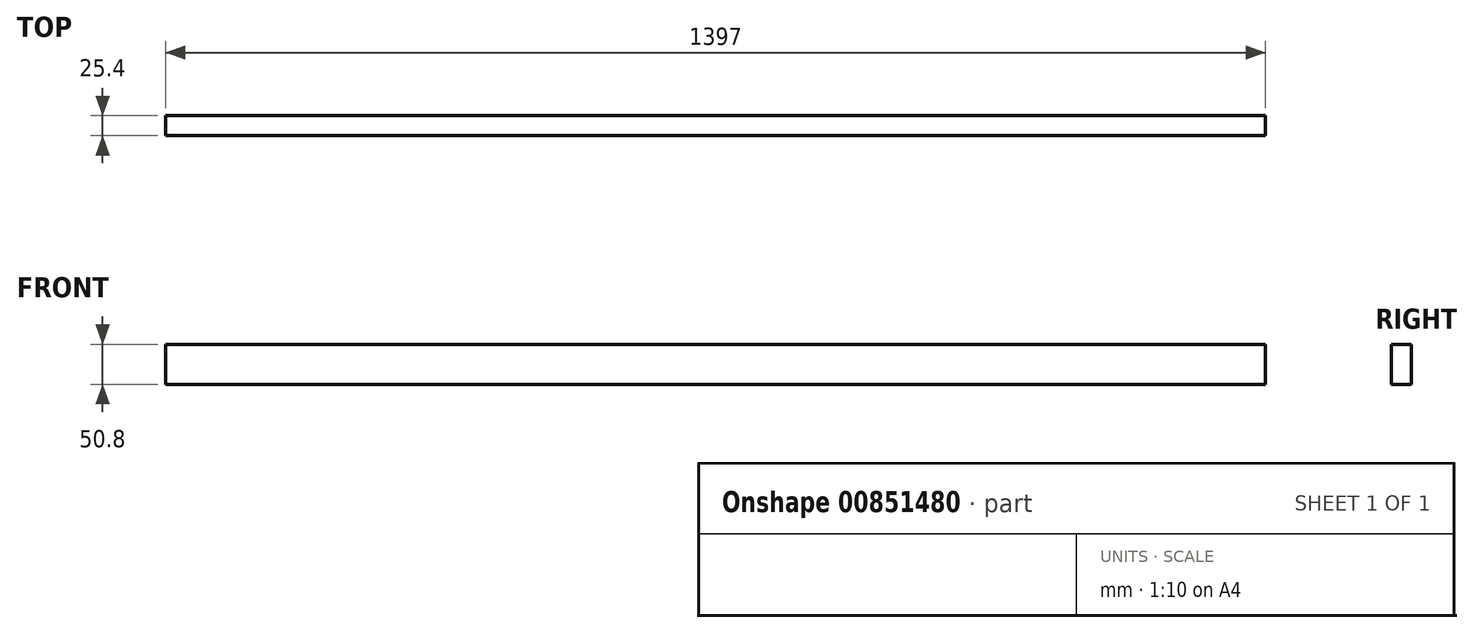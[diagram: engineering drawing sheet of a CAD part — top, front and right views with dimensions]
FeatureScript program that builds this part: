
annotation { "Feature Type Name" : "Feature", "Feature Type Description" : "" }
export const myFeature = defineFeature(function(context is Context, id is Id, definition is map)
    precondition{}
    {
        {
            var Q0;
            Q0=qCreatedBy(makeId("Front.planeOp"),FACE);
            var sketch = newSketch(context, id + "F0", { "sketchPlane" : qUnion([Q0])});
            skLineSegment(sketch, "E0.bottom", {"start": v(-304.8, 29.45) * mm, "end": v(1092.2, 29.45) * mm});
            skLineSegment(sketch, "E0.top", {"start": v(-304.8, -21.35) * mm, "end": v(1092.2, -21.35) * mm});
            skLineSegment(sketch, "E0.left", {"start": v(-304.8, 29.45) * mm, "end": v(-304.8, -21.35) * mm});
            skLineSegment(sketch, "E0.right", {"start": v(1092.2, 29.45) * mm, "end": v(1092.2, -21.35) * mm});
            skSolve(sketch);
        }
        {
            var Q0;
            Q0 = qSketchRegion(id + "F0", true);
            extrude(context, id + "F1", {"entities" : qUnion([Q0]), "depth" : 25.4 * mm, "offsetDistance" : 25.4 * mm});
        }
    });
